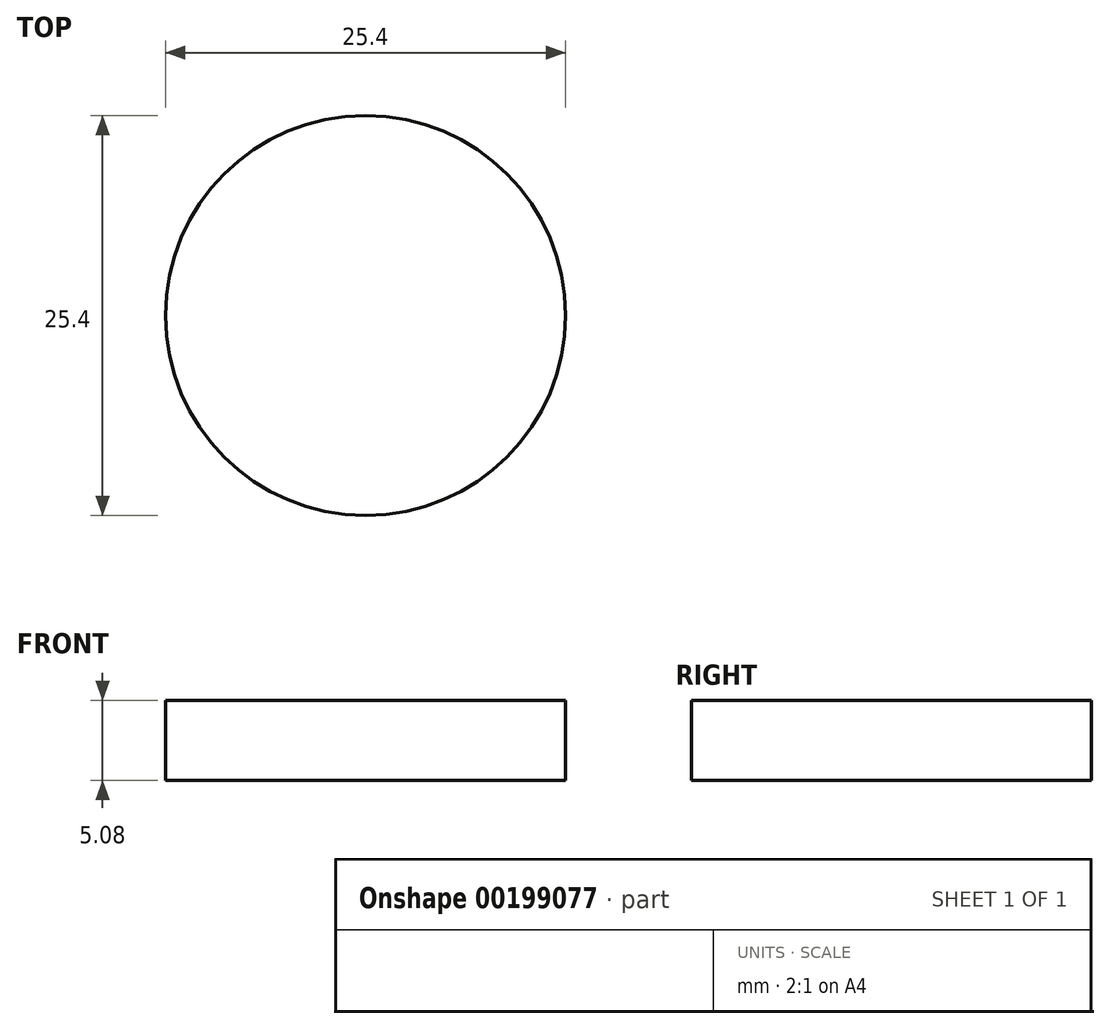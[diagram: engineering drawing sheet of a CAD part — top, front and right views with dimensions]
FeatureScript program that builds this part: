
annotation { "Feature Type Name" : "Feature", "Feature Type Description" : "" }
export const myFeature = defineFeature(function(context is Context, id is Id, definition is map)
    precondition{}
    {
        {
            var Q0;
            Q0=qCreatedBy(makeId("Top.planeOp"),FACE);
            var sketch = newSketch(context, id + "F0", { "sketchPlane" : qUnion([Q0])});
            skCircle(sketch, "E0", {"center": v(0, 0) * mm, "radius": 12.7 * mm});
            skSolve(sketch);
        }
        {
            var Q0;
            Q0=makeQuery(id+"F0.imprint","IMPRINT",FACE,{"disambiguationData":[TD([[makeQuery(id+"F0.imprint","IMPRINT",EDGE,{"derivedFrom":sQuery(id+"F0.wireOp",EDGE,"E0")}),1.0]])]});
            extrude(context, id + "F1", {"entities" : qUnion([Q0]), "depth" : 5.08 * mm});
        }
    });
